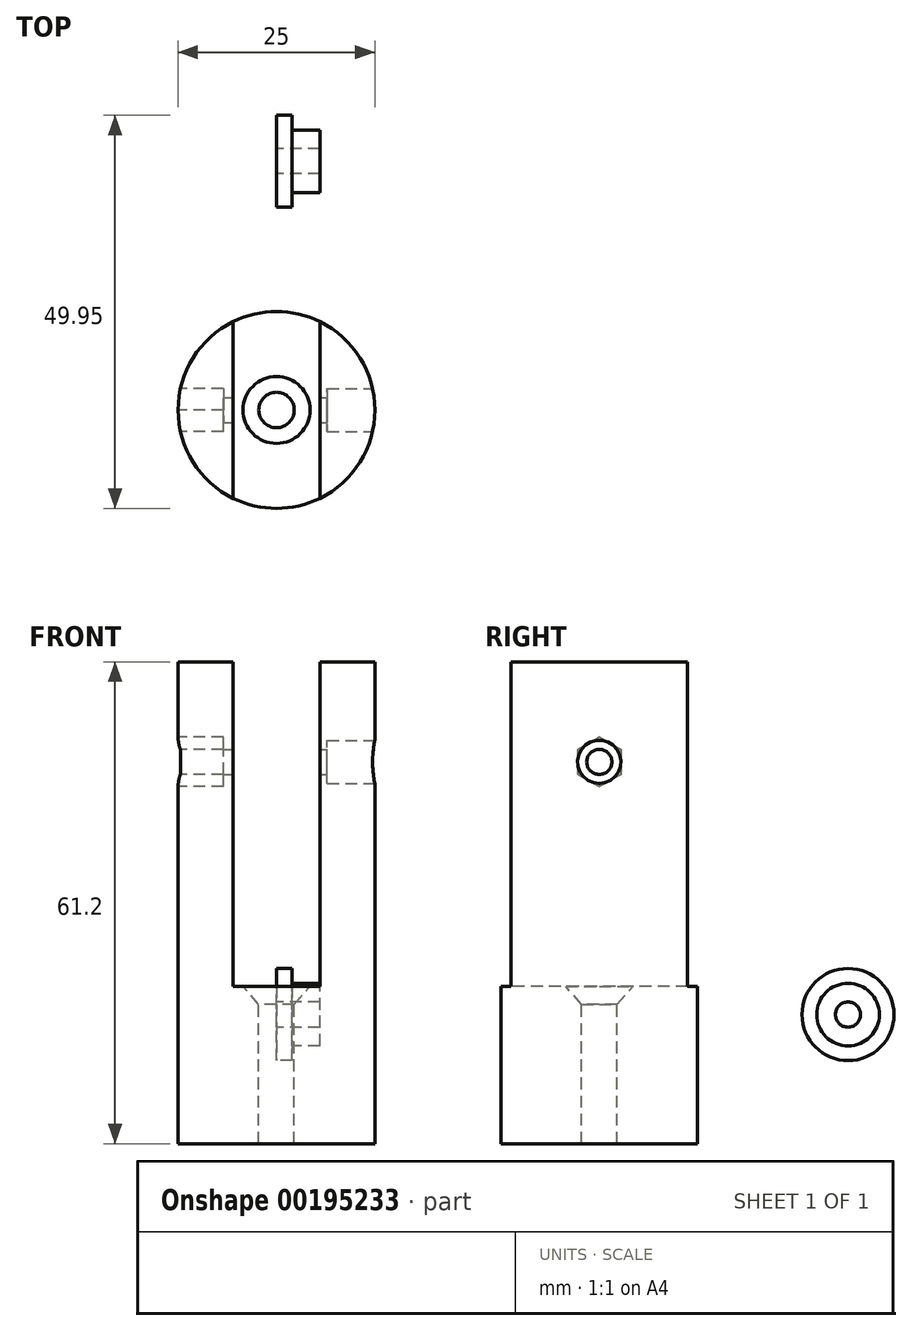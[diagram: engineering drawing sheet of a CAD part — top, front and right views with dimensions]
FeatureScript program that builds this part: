
annotation { "Feature Type Name" : "Feature", "Feature Type Description" : "" }
export const myFeature = defineFeature(function(context is Context, id is Id, definition is map)
    precondition{}
    {
        {
            var Q0;
            Q0=qCreatedBy(makeId("Top.planeOp"),FACE);
            var sketch = newSketch(context, id + "F0", { "sketchPlane" : qUnion([Q0])});
            skCircle(sketch, "E0", {"center": v(0, 0) * mm, "radius": 12.5 * mm});
            skSolve(sketch);
        }
        {
            var Q0;
            Q0 = qSketchRegion(id + "F0", true);
            extrude(context, id + "F1", {"entities" : qUnion([Q0]), "depth" : 61.2 * mm});
        }
        {
            var Q0;
            Q0=qCreatedBy(makeId("Front.planeOp"),FACE);
            var sketch = newSketch(context, id + "F2", { "sketchPlane" : qUnion([Q0])});
            skLineSegment(sketch, "E1.bottom", {"start": v(5.5, 61.2) * mm, "end": v(-5.5, 61.2) * mm});
            skLineSegment(sketch, "E1.top", {"start": v(5.5, 20) * mm, "end": v(-5.5, 20) * mm});
            skLineSegment(sketch, "E1.left", {"start": v(5.5, 61.2) * mm, "end": v(5.5, 20) * mm});
            skLineSegment(sketch, "E1.right", {"start": v(-5.5, 61.2) * mm, "end": v(-5.5, 20) * mm});
            skLineSegment(sketch, "E2", {"start": v(-12.5, 0) * mm, "end": v(-12.5, 61.2) * mm});
            skLineSegment(sketch, "E3", {"start": v(12.5, 61.2) * mm, "end": v(12.5, 0) * mm});
            skSolve(sketch);
        }
        {
            var Q0;
            Q0 = qSketchRegion(id + "F2", true);
            extrude(context, id + "F3", {"entities" : qUnion([Q0]), "operationType" : NewBodyOperationType.REMOVE, "endBound" : BoundingType.SYMMETRIC, "oppositeDirection" : true, "depth" : 25 * mm});
        }
        {
            var Q0;
            Q0=makeQuery(id+"F3.boolean.opBoolean","COPY",FACE,{"derivedFrom":makeQuery(id+"F3.opExtrude","SWEPT_FACE",FACE,{"disambiguationData":[OSD([sQuery(id+"F2.wireOp",EDGE,"E1.top")])]})});
            var sketch = newSketch(context, id + "F4", { "sketchPlane" : qUnion([Q0])});
            skPoint(sketch, "E4", {"position": v(0, 0) * mm});
            skSolve(sketch);
        }
        {
            var Q0;
            Q0=sQuery(id+"F4.wireOp",VERTEX,"E4");
            var Q1;
            Q1=makeQuery(id+"F1.opExtrude","SWEPT_BODY",BODY,{"disambiguationData":[OSD([sQuery(id+"F0.wireOp",EDGE,"E0")])]});
            hole(context, id + "F5", {"style" : HoleStyle.C_SINK, "endStyle" : HoleEndStyle.THROUGH, "holeDiameter" : 4.5 * mm, "cSinkDiameter" : 8.5 * mm, "cSinkAngle" : 82 * degree, "locations" : qUnion([Q0]), "scope" : qUnion([Q1]), "isTappedThrough" : true});
        }
        {
            var Q0;
            {var subQ0=sQuery(id+"F0.wireOp",EDGE,"E0");Q0=makeQuery(id+"F3.boolean.opBoolean","SPLIT",EDGE,{"disambiguationData":[TD([makeQuery(id+"F3.opExtrude","SWEPT_FACE",FACE,{"disambiguationData":[OSD([sQuery(id+"F2.wireOp",EDGE,"E1.left")])]})])],"derivedFrom":makeQuery(id+"F1.opExtrude","CAP_EDGE",EDGE,{"disambiguationData":[OSD([subQ0])],"isStart":false})});}
            cPoint(context, id + "F6", {"entities" : qUnion([Q0]), "parameter" : 0.5});
        }
        {
            var Q0;
            Q0 = qCreatedBy(id + "F6" ,VERTEX);
            var Q1;
            Q1=qCreatedBy(makeId("Right.planeOp"),FACE);
            cPlane(context, id + "F7", {"entities" : qUnion([Q0, Q1]), "cplaneType" : CPlaneType.PLANE_POINT, "offset" : 25 * mm, "width" : 150 * mm, "height" : 150 * mm});
        }
        {
            var Q0;
            Q0=qCreatedBy(id+"F7.planeOp",FACE);
            var sketch = newSketch(context, id + "F8", { "sketchPlane" : qUnion([Q0])});
            skPoint(sketch, "E5", {"position": v(0, 48.5) * mm});
            skSolve(sketch);
        }
        {
            var Q0;
            Q0=sQuery(id+"F8.wireOp",VERTEX,"E5");
            var Q1;
            Q1=makeQuery(id+"F1.opExtrude","SWEPT_BODY",BODY,{"disambiguationData":[OSD([sQuery(id+"F0.wireOp",EDGE,"E0")])]});
            hole(context, id + "F9", {"style" : HoleStyle.C_BORE, "endStyle" : HoleEndStyle.THROUGH, "holeDiameter" : 3.2 * mm, "cBoreDiameter" : 5.5 * mm, "cBoreDepth" : 5.75 * mm, "locations" : qUnion([Q0]), "scope" : qUnion([Q1]), "isTappedThrough" : true});
        }
        {
            var Q0;
            {var subQ0=sQuery(id+"F0.wireOp",EDGE,"E0");Q0=makeQuery(id+"F3.boolean.opBoolean","SPLIT",EDGE,{"disambiguationData":[TD([makeQuery(id+"F3.opExtrude","SWEPT_FACE",FACE,{"disambiguationData":[OSD([sQuery(id+"F2.wireOp",EDGE,"E1.right")])]})])],"derivedFrom":makeQuery(id+"F1.opExtrude","CAP_EDGE",EDGE,{"disambiguationData":[OSD([subQ0])],"isStart":false})});}
            cPoint(context, id + "F10", {"entities" : qUnion([Q0]), "parameter" : 0.5});
        }
        {
            var Q0;
            Q0 = qCreatedBy(id + "F10" ,VERTEX);
            var Q1;
            Q1=qCreatedBy(makeId("Right.planeOp"),FACE);
            cPlane(context, id + "F11", {"entities" : qUnion([Q0, Q1]), "cplaneType" : CPlaneType.PLANE_POINT, "offset" : 25 * mm, "width" : 150 * mm, "height" : 150 * mm});
        }
        {
            var Q0;
            Q0=qCreatedBy(id+"F11.planeOp",FACE);
            var sketch = newSketch(context, id + "F12", { "sketchPlane" : qUnion([Q0])});
            skPoint(sketch, "E6", {"position": v(0, 48.5) * mm});
            skCircle(sketch, "E7.cCircle", {"center": v(0, 48.5) * mm, "radius": 2.73 * mm, "construction": true});
            skLineSegment(sketch, "E7.0", {"start": v(-2.72, 50.07) * mm, "end": v(0, 51.65) * mm});
            skLineSegment(sketch, "E7.1", {"start": v(0, 51.65) * mm, "end": v(2.73, 50.07) * mm});
            skLineSegment(sketch, "E7.2", {"start": v(2.73, 50.07) * mm, "end": v(2.72, 46.93) * mm});
            skLineSegment(sketch, "E7.3", {"start": v(2.72, 46.93) * mm, "end": v(0, 45.35) * mm});
            skLineSegment(sketch, "E7.4", {"start": v(0, 45.35) * mm, "end": v(-2.73, 46.93) * mm});
            skLineSegment(sketch, "E7.5", {"start": v(-2.73, 46.93) * mm, "end": v(-2.72, 50.07) * mm});
            skPoint(sketch, "E7.0.midPoint", {"position": v(-1.36, 50.86) * mm});
            skCircle(sketch, "E8.0", {"center": v(0, 48.5) * mm, "radius": 1.6 * mm});
            skSolve(sketch);
        }
        {
            var Q0;
            Q0=makeQuery(id+"F12.imprint","IMPRINT",FACE,{"disambiguationData":[TD([[makeQuery(id+"F12.imprint","IMPRINT",EDGE,{"derivedFrom":sQuery(id+"F12.wireOp",EDGE,"E7.0")}),-1.0]])]});
            extrude(context, id + "F13", {"entities" : qUnion([Q0]), "operationType" : NewBodyOperationType.REMOVE, "depth" : 5.75 * mm});
        }
        {
            var Q0;
            Q0=qCreatedBy(makeId("Right.planeOp"),FACE);
            var sketch = newSketch(context, id + "F14", { "sketchPlane" : qUnion([Q0])});
            skCircle(sketch, "E9", {"center": v(31.6, 16.4) * mm, "radius": 5.85 * mm});
            skCircle(sketch, "E10", {"center": v(31.6, 16.4) * mm, "radius": 1.6 * mm});
            skSolve(sketch);
        }
        {
            var Q0;
            Q0=makeQuery(id+"F14.imprint","IMPRINT",FACE,{"disambiguationData":[TD([[makeQuery(id+"F14.imprint","IMPRINT",EDGE,{"derivedFrom":sQuery(id+"F14.wireOp",EDGE,"E9")}),1.0]])]});
            extrude(context, id + "F15", {"entities" : qUnion([Q0]), "depth" : 2 * mm});
        }
        {
            var Q0;
            Q0=makeQuery(id+"F15.opExtrude","CAP_FACE",FACE,{"disambiguationData":[OSD([sQuery(id+"F14.wireOp",EDGE,"E9"),sQuery(id+"F14.wireOp",EDGE,"E10")])],"isStart":false});
            var sketch = newSketch(context, id + "F16", { "sketchPlane" : qUnion([Q0])});
            skCircle(sketch, "E11", {"center": v(31.6, 16.4) * mm, "radius": 3.98 * mm});
            skSolve(sketch);
        }
        {
            var Q0;
            Q0=makeQuery(id+"F16.imprint","IMPRINT",FACE,{"disambiguationData":[TD([[makeQuery(id+"F16.imprint","IMPRINT",EDGE,{"derivedFrom":sQuery(id+"F16.wireOp",EDGE,"E11")}),1.0]])]});
            extrude(context, id + "F17", {"entities" : qUnion([Q0]), "operationType" : NewBodyOperationType.ADD, "depth" : 3.5 * mm});
        }
    });
